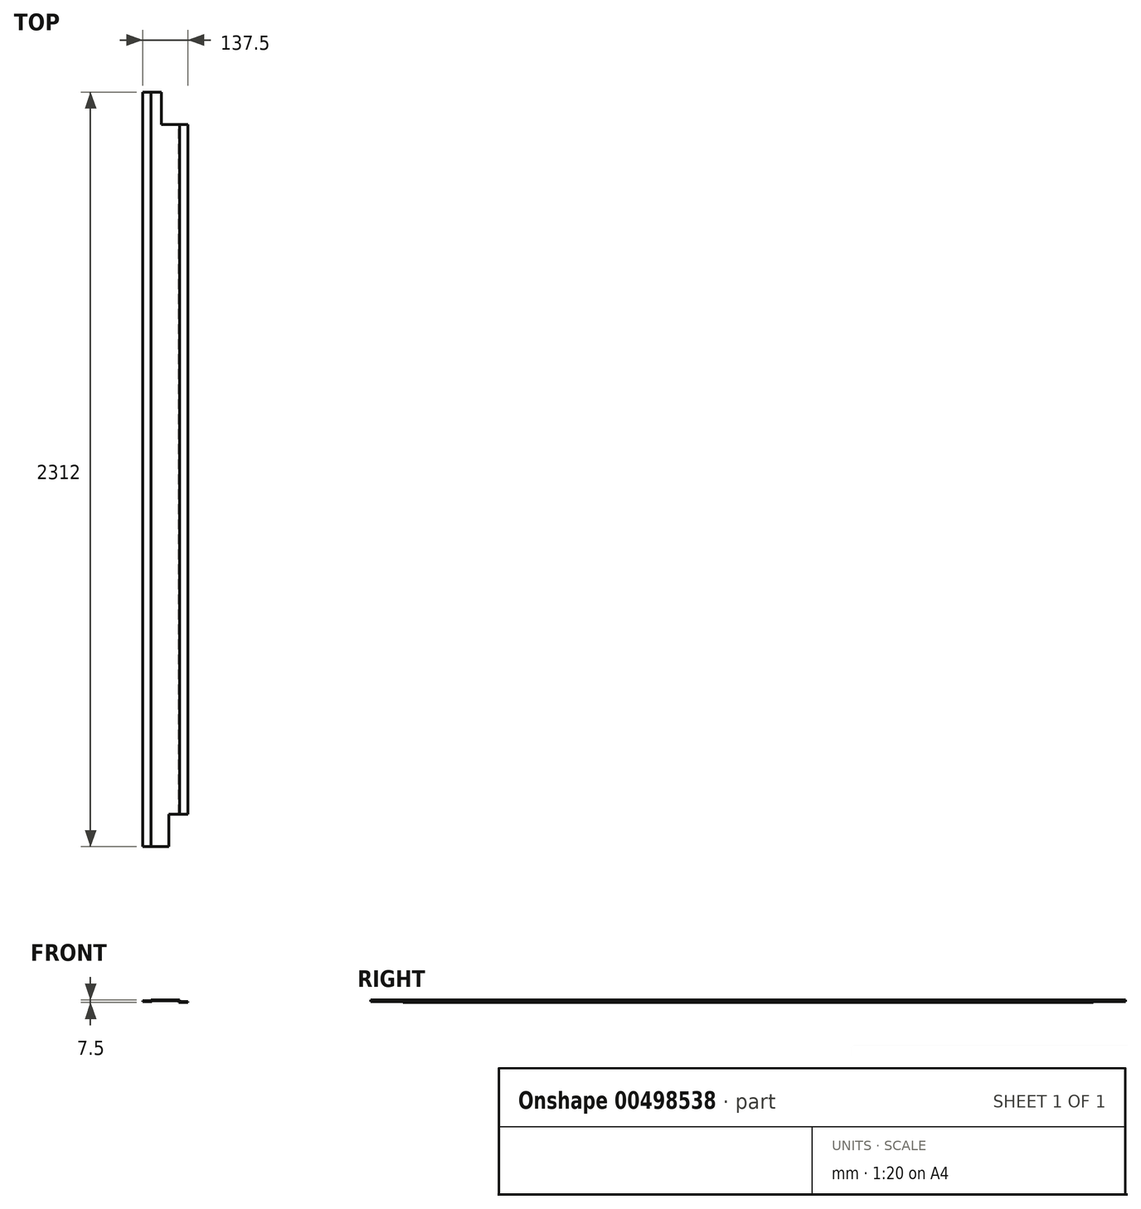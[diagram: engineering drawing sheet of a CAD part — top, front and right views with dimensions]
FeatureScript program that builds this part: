
annotation { "Feature Type Name" : "Feature", "Feature Type Description" : "" }
export const myFeature = defineFeature(function(context is Context, id is Id, definition is map)
    precondition{}
    {
        {
            var Q0;
            Q0=qCreatedBy(makeId("Front.planeOp"),FACE);
            var sketch = newSketch(context, id + "F0", { "sketchPlane" : qUnion([Q0])});
            skLineSegment(sketch, "E0", {"start": v(0, 0) * mm, "end": v(87.5, 0) * mm});
            skLineSegment(sketch, "E1", {"start": v(87.5, 0) * mm, "end": v(87.5, -5) * mm});
            skLineSegment(sketch, "E2", {"start": v(87.5, -5) * mm, "end": v(112.5, -5) * mm});
            skLineSegment(sketch, "E3", {"start": v(0, 0) * mm, "end": v(0, -2) * mm});
            skLineSegment(sketch, "E4", {"start": v(0, -2) * mm, "end": v(-25, -2) * mm});
            skLineSegment(sketch, "E5.0", {"start": v(2.5, -4.5) * mm, "end": v(-25, -4.5) * mm});
            skLineSegment(sketch, "E5.1", {"start": v(85, -7.5) * mm, "end": v(112.5, -7.5) * mm});
            skLineSegment(sketch, "E5.2", {"start": v(85, -2.5) * mm, "end": v(85, -7.5) * mm});
            skLineSegment(sketch, "E5.3", {"start": v(2.5, -2.5) * mm, "end": v(85, -2.5) * mm});
            skLineSegment(sketch, "E5.4", {"start": v(2.5, -2.5) * mm, "end": v(2.5, -4.5) * mm});
            skLineSegment(sketch, "E6", {"start": v(-25, -2) * mm, "end": v(-25, -4.5) * mm});
            skLineSegment(sketch, "E7", {"start": v(112.5, -5) * mm, "end": v(112.5, -7.5) * mm});
            skSolve(sketch);
        }
        {
            var Q0;
            Q0=makeQuery(id+"F0.imprint","IMPRINT",FACE,{"disambiguationData":[TD([[makeQuery(id+"F0.imprint","IMPRINT",EDGE,{"derivedFrom":sQuery(id+"F0.wireOp",EDGE,"E0")}),-1.0]])]});
            extrude(context, id + "F1", {"entities" : qUnion([Q0]), "depth" : 2312 * mm});
        }
        {
            var Q0;
            Q0=makeQuery(id+"F1.opExtrude","SWEPT_FACE",FACE,{"disambiguationData":[OSD([sQuery(id+"F0.wireOp",EDGE,"E0")])]});
            var sketch = newSketch(context, id + "F2", { "sketchPlane" : qUnion([Q0])});
            skLineSegment(sketch, "E8", {"start": v(87.5, -1156) * mm, "end": v(0, -1156) * mm});
            skLineSegment(sketch, "E9.MirrorCS", {"start": v(87.5, 0) * mm, "end": v(112.5, 0) * mm});
            skLineSegment(sketch, "E10.MirrorCS", {"start": v(31.27, 0) * mm, "end": v(31.27, -99) * mm});
            skLineSegment(sketch, "E11.MirrorCS", {"start": v(112.5, 0) * mm, "end": v(31.27, 0) * mm});
            skLineSegment(sketch, "E12.MirrorCS", {"start": v(112.5, -99) * mm, "end": v(112.5, 0) * mm});
            skLineSegment(sketch, "E13.MirrorCS", {"start": v(31.27, -99) * mm, "end": v(112.5, -99) * mm});
            skLineSegment(sketch, "E14", {"start": v(54, -2312) * mm, "end": v(54, -2213) * mm});
            skLineSegment(sketch, "E15", {"start": v(54, -2213) * mm, "end": v(127.14, -2213) * mm});
            skLineSegment(sketch, "E16", {"start": v(127.14, -2213) * mm, "end": v(127.14, -2342.16) * mm});
            skLineSegment(sketch, "E17", {"start": v(127.14, -2342.16) * mm, "end": v(54, -2342.16) * mm});
            skLineSegment(sketch, "E18", {"start": v(54, -2342.16) * mm, "end": v(54, -2312) * mm});
            skSolve(sketch);
        }
        {
            var Q0;
            {var subQ0=sQuery(id+"F2.wireOp",EDGE,"E10.MirrorCS");Q0=makeQuery(id+"F2.imprint","IMPRINT",FACE,{"disambiguationData":[TD([[makeQuery(id+"F2.imprint","IMPRINT",EDGE,{"derivedFrom":subQ0}),1.0]])]});}
            var Q1;
            {var subQ3=sQuery(id+"F2.wireOp",EDGE,"E12.MirrorCS");Q1=makeQuery(id+"F2.imprint","IMPRINT",FACE,{"disambiguationData":[TD([[makeQuery(id+"F2.imprint","IMPRINT",EDGE,{"derivedFrom":subQ3}),1.0]])]});}
            var Q2;
            {var subQ4=sQuery(id+"F2.wireOp",EDGE,"wxqYpE2Q-F7i4-i0FH-CTGg-dDkOMMLiui6R");Q2=makeQuery(id+"F2.imprint","IMPRINT",FACE,{"disambiguationData":[TD([[makeQuery(id+"F2.imprint","IMPRINT",EDGE,{"derivedFrom":subQ4}),-1.0]])]});}
            var Q3;
            {var subQ3=sQuery(id+"F2.wireOp",EDGE,"5ZFSIXGI-Wiv1-SM6m-rBuU-2osIjjbjvH1q");Q3=makeQuery(id+"F2.imprint","IMPRINT",FACE,{"disambiguationData":[TD([[makeQuery(id+"F2.imprint","IMPRINT",EDGE,{"derivedFrom":subQ3}),-1.0]])]});}
            var Q4;
            {var subQ1=sQuery(id+"F2.wireOp",EDGE,"E16");Q4=makeQuery(id+"F2.imprint","IMPRINT",FACE,{"disambiguationData":[TD([[makeQuery(id+"F2.imprint","IMPRINT",EDGE,{"derivedFrom":subQ1}),-1.0]])]});}
            var Q5;
            {var subQ0=sQuery(id+"F2.wireOp",EDGE,"E14");Q5=makeQuery(id+"F2.imprint","IMPRINT",FACE,{"disambiguationData":[TD([[makeQuery(id+"F2.imprint","IMPRINT",EDGE,{"derivedFrom":subQ0}),-1.0]])]});}
            extrude(context, id + "F3", {"entities" : qUnion([Q0, Q1, Q2, Q3, Q4, Q5]), "operationType" : NewBodyOperationType.REMOVE, "endBound" : BoundingType.THROUGH_ALL, "oppositeDirection" : true, "depth" : 25 * mm});
        }
    });
